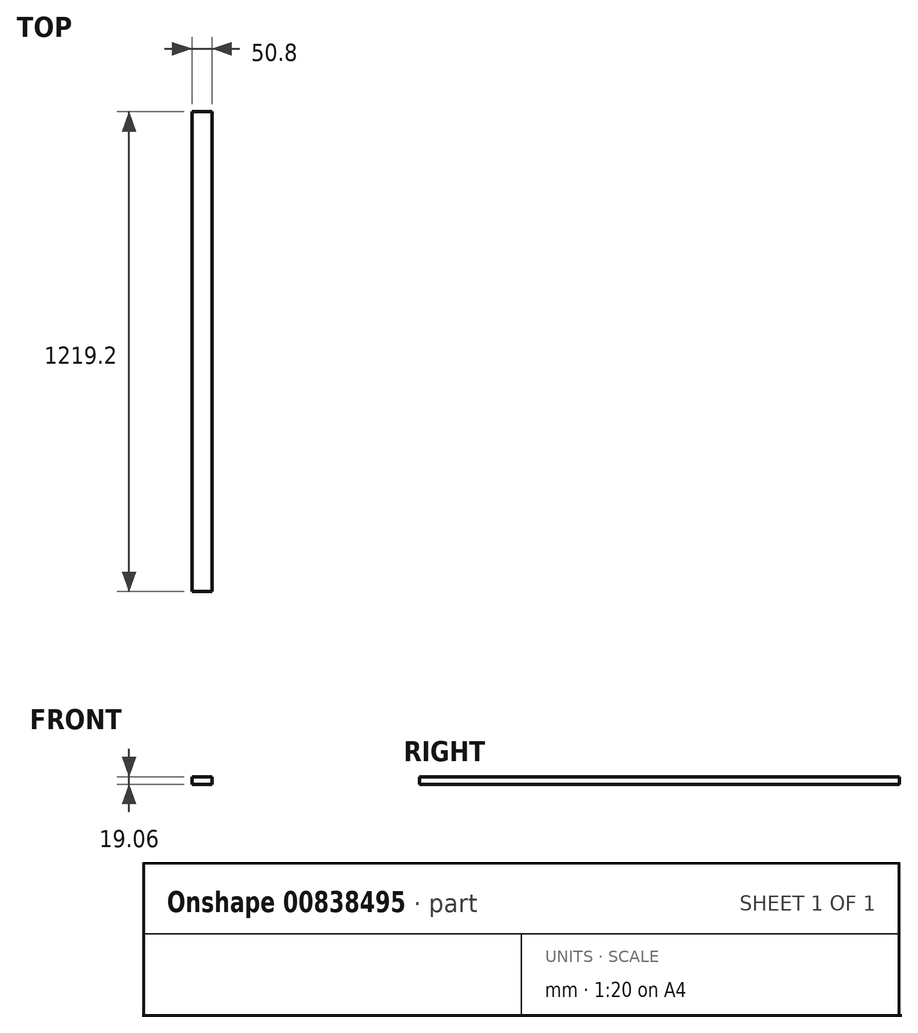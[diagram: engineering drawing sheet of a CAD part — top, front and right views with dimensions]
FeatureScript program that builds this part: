
annotation { "Feature Type Name" : "Feature", "Feature Type Description" : "" }
export const myFeature = defineFeature(function(context is Context, id is Id, definition is map)
    precondition{}
    {
        {
            var Q0;
            Q0=qCreatedBy(makeId("Right.planeOp"),FACE);
            var sketch = newSketch(context, id + "F0", { "sketchPlane" : qUnion([Q0])});
            skLineSegment(sketch, "E0.bottom", {"start": v(-609.6, -9.53) * mm, "end": v(609.6, -9.53) * mm});
            skLineSegment(sketch, "E0.top", {"start": v(-609.6, 9.53) * mm, "end": v(609.6, 9.53) * mm});
            skLineSegment(sketch, "E0.left", {"start": v(-609.6, -9.53) * mm, "end": v(-609.6, 9.53) * mm});
            skLineSegment(sketch, "E0.right", {"start": v(609.6, -9.53) * mm, "end": v(609.6, 9.53) * mm});
            skPoint(sketch, "E0.middle", {"position": v(0, 0) * mm});
            skSolve(sketch);
        }
        {
            var Q0;
            Q0=makeQuery(id+"F0.imprint","IMPRINT",FACE,{"disambiguationData":[TD([[makeQuery(id+"F0.imprint","IMPRINT",EDGE,{"derivedFrom":sQuery(id+"F0.wireOp",EDGE,"E0.bottom")}),1.0]])]});
            extrude(context, id + "F1", {"entities" : qUnion([Q0]), "depth" : 50.8 * mm, "offsetDistance" : 25.4 * mm});
        }
    });
